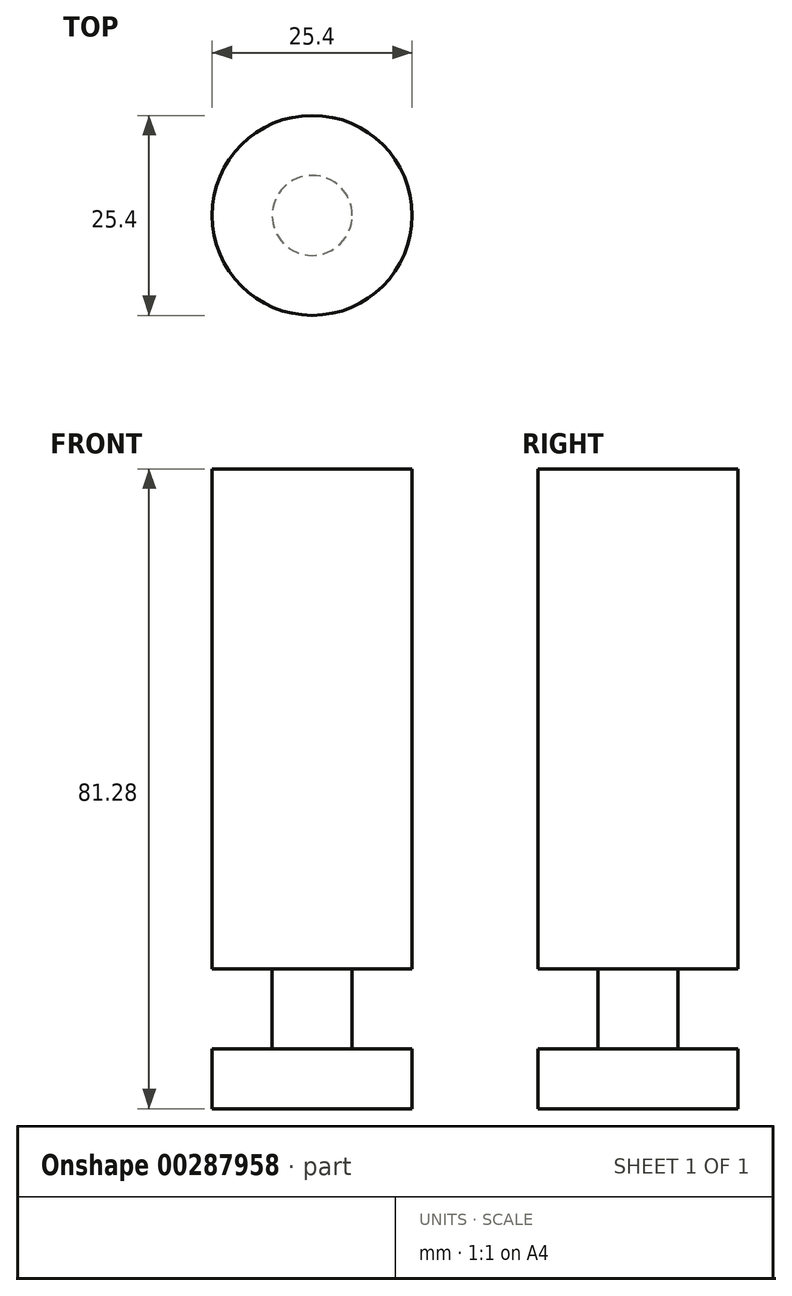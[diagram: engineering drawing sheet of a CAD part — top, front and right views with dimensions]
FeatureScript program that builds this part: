
annotation { "Feature Type Name" : "Feature", "Feature Type Description" : "" }
export const myFeature = defineFeature(function(context is Context, id is Id, definition is map)
    precondition{}
    {
        {
            var Q0;
            Q0=qCreatedBy(makeId("Top.planeOp"),FACE);
            var sketch = newSketch(context, id + "F0", { "sketchPlane" : qUnion([Q0])});
            skCircle(sketch, "E0", {"center": v(-48.28, 12.8) * mm, "radius": 12.7 * mm});
            skSolve(sketch);
        }
        {
            var Q0;
            Q0=makeQuery(id+"F0.imprint","IMPRINT",FACE,{"disambiguationData":[TD([[makeQuery(id+"F0.imprint","IMPRINT",EDGE,{"derivedFrom":sQuery(id+"F0.wireOp",EDGE,"E0")}),1.0]])]});
            extrude(context, id + "F1", {"entities" : qUnion([Q0]), "depth" : 63.5 * mm});
        }
        {
            var Q0;
            Q0=makeQuery(id+"F1.opExtrude","CAP_FACE",FACE,{"disambiguationData":[OSD([sQuery(id+"F0.wireOp",EDGE,"E0")])],"isStart":true});
            var sketch = newSketch(context, id + "F2", { "sketchPlane" : qUnion([Q0])});
            skCircle(sketch, "E1", {"center": v(-48.28, -12.8) * mm, "radius": 5.08 * mm});
            skSolve(sketch);
        }
        {
            var Q0;
            Q0=makeQuery(id+"F2.imprint","IMPRINT",FACE,{"disambiguationData":[TD([[makeQuery(id+"F2.imprint","IMPRINT",EDGE,{"derivedFrom":sQuery(id+"F2.wireOp",EDGE,"E1")}),1.0]])]});
            extrude(context, id + "F3", {"entities" : qUnion([Q0]), "operationType" : NewBodyOperationType.ADD, "depth" : 10.16 * mm});
        }
        {
            var Q0;
            Q0=makeQuery(id+"F3.opExtrude","CAP_FACE",FACE,{"disambiguationData":[OSD([sQuery(id+"F2.wireOp",EDGE,"E1")])],"isStart":false});
            var sketch = newSketch(context, id + "F4", { "sketchPlane" : qUnion([Q0])});
            skCircle(sketch, "E2", {"center": v(-48.28, -12.8) * mm, "radius": 12.7 * mm});
            skSolve(sketch);
        }
        {
            var Q0;
            Q0=makeQuery(id+"F4.imprint","IMPRINT",FACE,{"disambiguationData":[TD([[makeQuery(id+"F4.imprint","IMPRINT",EDGE,{"derivedFrom":sQuery(id+"F4.wireOp",EDGE,"E2")}),1.0]])]});
            var Q1;
            Q1=makeQuery(id+"F4.imprint","IMPRINT",FACE,{"disambiguationData":[TD([[makeQuery(id+"F4.imprint","IMPRINT",EDGE,{"derivedFrom":makeQuery(id+"F3.opExtrude","CAP_EDGE",EDGE,{"disambiguationData":[OSD([sQuery(id+"F2.wireOp",EDGE,"E1")])],"isStart":false})}),1.0]])]});
            extrude(context, id + "F5", {"entities" : qUnion([Q0, Q1]), "operationType" : NewBodyOperationType.ADD, "depth" : 7.62 * mm});
        }
    });
